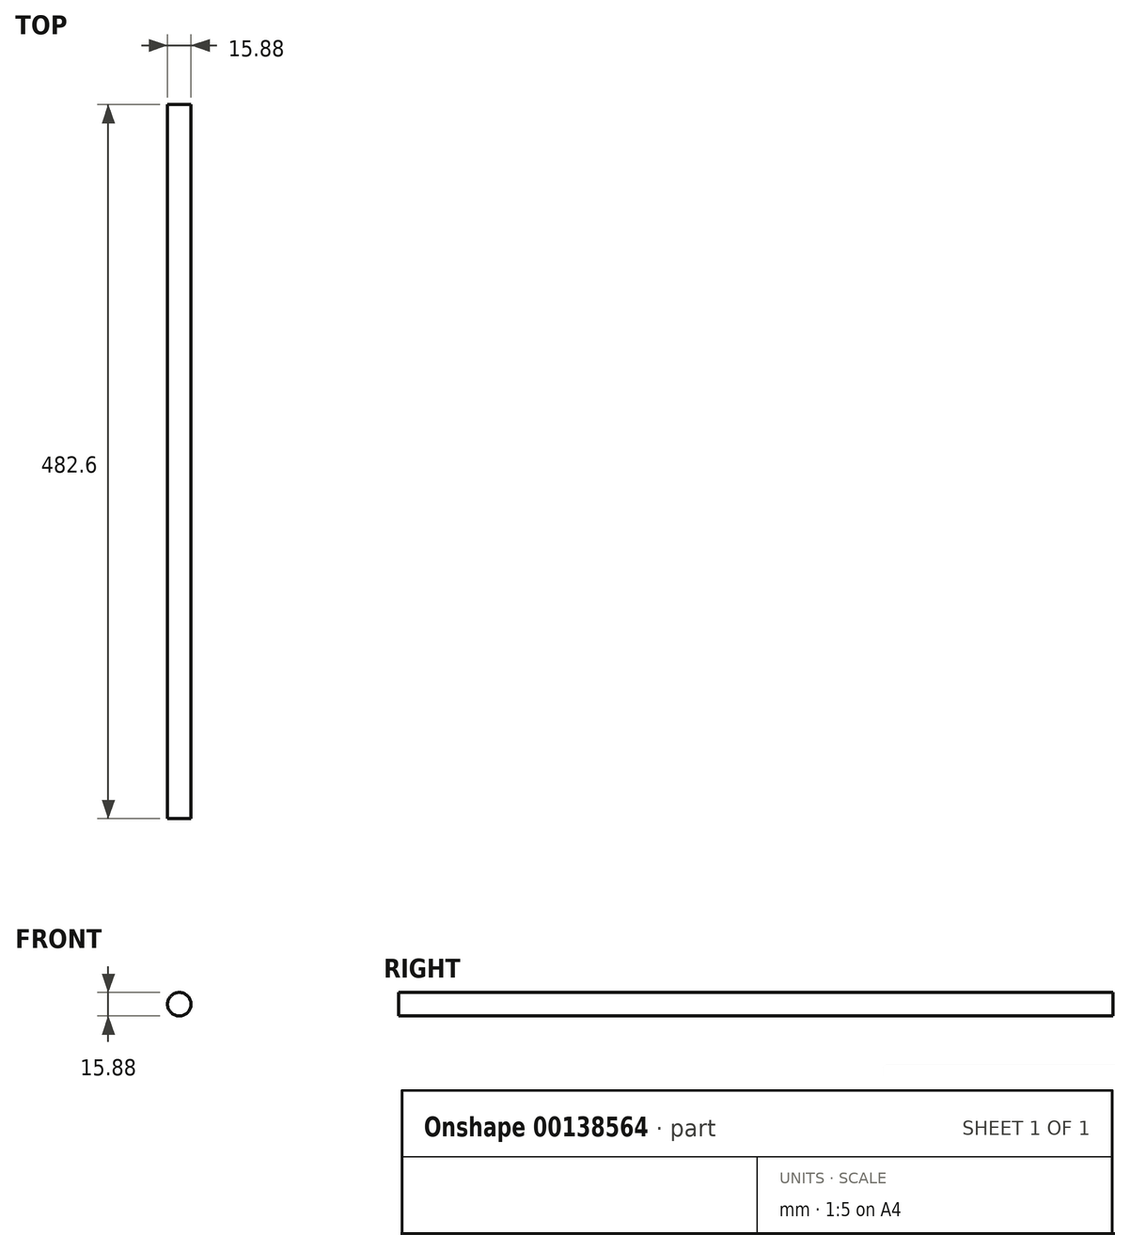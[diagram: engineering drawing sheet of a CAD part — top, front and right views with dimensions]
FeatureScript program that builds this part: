
annotation { "Feature Type Name" : "Feature", "Feature Type Description" : "" }
export const myFeature = defineFeature(function(context is Context, id is Id, definition is map)
    precondition{}
    {
        {
            var Q0;
            Q0=qCreatedBy(makeId("Front.planeOp"),FACE);
            var sketch = newSketch(context, id + "F0", { "sketchPlane" : qUnion([Q0])});
            skCircle(sketch, "E0", {"center": v(0, 0) * mm, "radius": 7.94 * mm});
            skSolve(sketch);
        }
        {
            var Q0;
            Q0=makeQuery(id+"F0.imprint","IMPRINT",FACE,{"disambiguationData":[TD([[makeQuery(id+"F0.imprint","IMPRINT",EDGE,{"derivedFrom":sQuery(id+"F0.wireOp",EDGE,"E0")}),1.0]])]});
            extrude(context, id + "F1", {"entities" : qUnion([Q0]), "depth" : 482.6 * mm});
        }
    });
